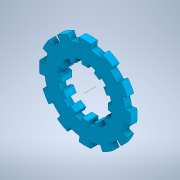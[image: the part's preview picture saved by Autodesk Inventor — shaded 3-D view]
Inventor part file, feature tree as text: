
AUTODESK INVENTOR PART (.ipt)
format: ipt  version: 2021.2 (Build 252289000, 289)  size: 291,328 bytes
history: native  units: in
note: dims shown in document units (in); Inventor stores cm internally (conversion verified against a paired STEP export)
features: reference x7, extrude x5, sketch x4, other x3, pattern_circular x2
ambient origin geometry x8: Origin, YZ Plane, XZ Plane, XY Plane, X Axis, Y Axis, Z Axis, Center Point
bodies: Solid1 (feature_tree)
feature tree (21):
  extrude  "Extrusion1"  Depth=0.25in TaperAngle=0.0deg
  extrude  "Extrusion3"  TaperAngle=0.0deg  [1 undecoded]
  extrude  "Extrusion8"  TaperAngle=15.0deg  [1 undecoded]
  pattern_circular  "Circular Pattern3"  Count=12  [1 undecoded]
  extrude  "Extrusion9"  TaperAngle=360.0deg  [1 undecoded]
  pattern_circular  "Circular Pattern4"  [2 undecoded]
  extrude  "Extrusion10"  TaperAngle=15.0deg  [1 undecoded]
  sketch  "Sketch1"  dims[d0=3.0in d1=0.25in d2=0.0in]
  sketch  "Sketch3"  dims[d8=2.0in d9=0.0in d10=0.0in]
  sketch  "Sketch8"  dims[d32=0.1309in d34=15.0deg]
  sketch  "Sketch9"  dims[d35=0.375in d36=0.0in d37=4.7244in d38=360.0deg d40=0.1963in d41=15.0deg d42=0.0515in d43=0.25in d44=0.0in d45=4.7244in d46=360.0deg d52=0.5in d53=0.25in d54=0.0in]
  reference  "Reference1"
  reference  "Reference2"
  reference  "Reference3"
  reference  "Reference4"
  reference  "Reference5"
  reference  "Reference6"
  reference  "Reference7"
  other  "SplineAssembly.iam"
  other  "connectorToTubeBracketWithOffsetHexShaft-V01:1"
  other  "centerPartOfLock:1"
note: 7 required parameter values undecoded (feature->parameter linkage not recoverable at this tier; creation-order binding heuristic only, values carry confidence <= 0.55)
